# Revit family: Haworth_ComposeStorage_Lateral
name_source: partatom
category: Furniture Systems
revit_build: Autodesk Revit 2018 (Build: 20170223_1515(x64)
units: mm (PartAtom-declared; Revit-internal decimal feet)

## family parameters
Always vertical = Yes
Cut with Voids When Loaded = No
OmniClass Number = 23.40.70.14.64.21
OmniClass Title = Systems Furniture
Part Type = Normal
Room Calculation Point = No
Round Connector Dimension = Use Diameter
Shared = No
Work Plane-Based = No

## types (6) — shared parameters
Actual Depth = 23"
Actual Width = 36"
Assembly Code = E2020200
Back Finish = Haworth _ Wood _ White Oak
Base = Yes
Base Finish = Haworth _ Wood _ White Oak
Base Height = 1"
Base Low = Yes
Cabinet Finish = Haworth _ Wood _ White Oak
Chamfer Legs = No
Classic Pull = No
Crescent Pull = No
Custom Size = No
Depth = 24"
Depth Adjuster = 1"
Description = Haworth - Compose Storage Lateral
Doors = No
Drawer Finish = Haworth _ Wood _ White Oak
Drawer Height Bottom = 13"
Drawer Height Top = 12"
Finished Back = Yes
J Pull = No
Linear Pull = No
Manufacturer = Haworth
Max. Depth = 24"
Max. Height = 40"
Max. Width = 36"
Min. Depth = 18"
Min. Height = 14"
Min. Width = 30"
Model = BZL
Patterns Pull = Yes
Plynth Base = No
Pull Finish = Haworth _ Metal _ Brushed Aluminum
Revision Number = 3
Side Panel Base = Yes
Size = Verify Final Dim. w/ Haworth
Spacer Finish = Haworth _ Wood _ White Oak
Spacer Height = 0"
Standard Depths = 18, 24 in.
Standard Height = 14 1/4, 20, 26 1/4, 38 1/4 in.
Standard Widths = 30, 36 in.
Sustainability Info = http://media.haworth.com
Top Spacer = No
URL = www.haworth.com
URL - Product = http://www.haworth.com
Warranty = http://www.haworth.com
Width = 36"

## per-type parameters (varying)
| type | Actual Height | Door Height | Drawer Height Middle | Drawer Two Off | Drawer Two On | One And A Half High | One High | Open Shelf Lateral | Shelf 1 | Shelf 1 Offset | Shelf 2 Offet | Three High | Two High |
| 3 High 36w 24d Full Lateral | 38 1/4" | 37 1/4" | 12" | No | Yes | No | No | No | No | 12 43/256" | 12 43/256" | Yes | No |
| 2 High 36w 24d Full Lateral | 26 1/4" | 25 1/4" | 12" | No | Yes | No | No | No | No | 12 5/8" | 8 43/256" | No | Yes |
| 1 High 36w 24d Full Lateral | 14 1/4" | 13 1/4" | 12" | No | No | No | Yes | No | No | 4 43/256" | 4 43/256" | No | No |
| 1.5 High 36w 24d Full Lateral | 22 1/4" | 21 1/4" | 8" | No | Yes | Yes | No | No | No | 6 213/256" | 6 213/256" | No | No |
| 2 High 36w 24d Open Shelf Lateral | 26 1/4" | 25 1/4" | 12" | Yes | No | No | No | Yes | Yes | 12 5/8" | 8 43/256" | No | Yes |
| 1.5 High 36w 24d Open Shelf Lateral | 22 1/4" | 21 1/4" | 8" | Yes | No | Yes | No | Yes | Yes | 6 213/256" | 6 213/256" | No | No |

## geometry (parser evidence)
native form markers: Sweep x14
no freeform markers — native parametric forms only
